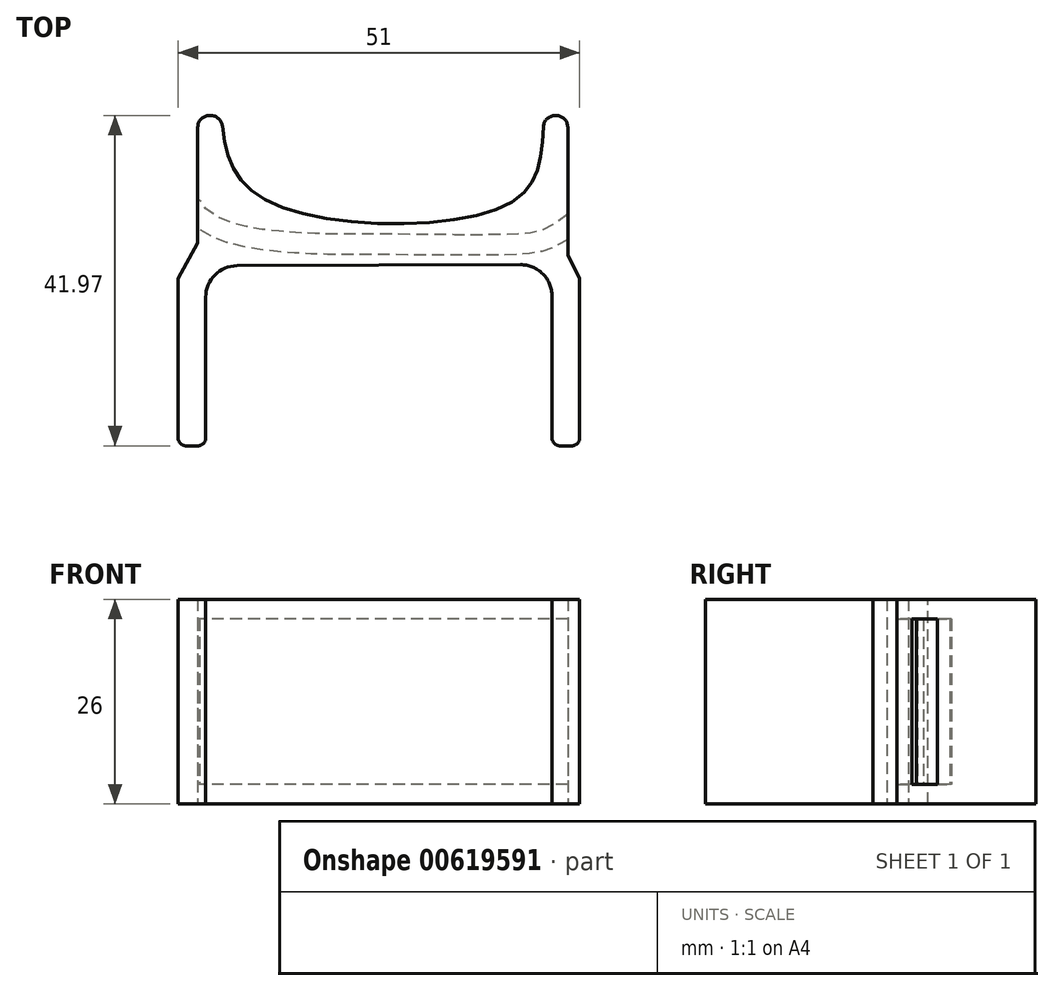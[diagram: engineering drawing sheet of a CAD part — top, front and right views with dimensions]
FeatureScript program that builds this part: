
annotation { "Feature Type Name" : "Feature", "Feature Type Description" : "" }
export const myFeature = defineFeature(function(context is Context, id is Id, definition is map)
    precondition{}
    {
        {
            var Q0;
            Q0=qCreatedBy(makeId("Top.planeOp"),FACE);
            var sketch = newSketch(context, id + "F0", { "sketchPlane" : qUnion([Q0])});
            skLineSegment(sketch, "E0.top", {"start": v(-21.5, 20.37) * mm, "end": v(19.5, 20.37) * mm});
            skPoint(sketch, "E0.middle", {"position": v(0, 0) * mm});
            skLineSegment(sketch, "E1.left", {"start": v(-15.5, 0) * mm, "end": v(-15.5, 9.44) * mm, "construction": true});
            skLineSegment(sketch, "E1.right", {"start": v(15.5, 0) * mm, "end": v(15.5, 9.44) * mm, "construction": true});
            skFitSpline(sketch, "E2", {"points": [v(19.5, 20.37) * mm, v(15.5, 9.44) * mm, v(-15.5, 9.44) * mm, v(-21.5, 20.37) * mm], "startDerivative": vector(-3.97, -51.43) * mm, "endDerivative": vector(-3.97, 51.43) * mm});
            skPoint(sketch, "E3.endSnap0", {"position": v(-22, 0) * mm});
            skLineSegment(sketch, "E4", {"start": v(-26.98, -0.36) * mm, "end": v(-26.98, -20.6) * mm});
            skLineSegment(sketch, "E5", {"start": v(-25.98, -21.6) * mm, "end": v(-24.48, -21.6) * mm});
            skLineSegment(sketch, "E6", {"start": v(24.02, -20.6) * mm, "end": v(24.02, -0.36) * mm});
            skLineSegment(sketch, "E7", {"start": v(20.52, -20.6) * mm, "end": v(20.52, -2.59) * mm});
            skLineSegment(sketch, "E8", {"start": v(16.5, 1.41) * mm, "end": v(-19.5, 1.28) * mm});
            skLineSegment(sketch, "E9", {"start": v(-23.48, -2.72) * mm, "end": v(-23.48, -20.6) * mm});
            skLineSegment(sketch, "E10.trimOffspring", {"start": v(21.52, -21.6) * mm, "end": v(23.02, -21.6) * mm});
            skPoint(sketch, "E11.visualSharp", {"position": v(-23.48, 1.26) * mm});
            skArc(sketch, "E11.filletArc", {"start": v(-19.5, 1.28) * mm, "mid": v(-22.32, 0.1) * mm, "end": v(-23.48, -2.72) * mm});
            skPoint(sketch, "E12.visualSharp", {"position": v(20.52, 1.43) * mm});
            skArc(sketch, "E12.filletArc", {"start": v(20.52, -2.59) * mm, "mid": v(19.34, 0.25) * mm, "end": v(16.5, 1.41) * mm});
            skPoint(sketch, "E13.visualSharp", {"position": v(-23.48, -21.6) * mm});
            skArc(sketch, "E13.filletArc", {"start": v(-24.48, -21.6) * mm, "mid": v(-23.78, -21.3) * mm, "end": v(-23.48, -20.6) * mm});
            skPoint(sketch, "E14.visualSharp", {"position": v(20.52, -21.6) * mm});
            skArc(sketch, "E14.filletArc", {"start": v(20.52, -20.6) * mm, "mid": v(20.8, -21.3) * mm, "end": v(21.52, -21.6) * mm});
            skPoint(sketch, "E15.visualSharp", {"position": v(-26.98, -21.6) * mm});
            skArc(sketch, "E15.filletArc", {"start": v(-26.98, -20.6) * mm, "mid": v(-26.7, -21.3) * mm, "end": v(-25.98, -21.6) * mm});
            skPoint(sketch, "E16.visualSharp", {"position": v(24.02, -21.6) * mm});
            skArc(sketch, "E16.filletArc", {"start": v(23.02, -21.6) * mm, "mid": v(23.72, -21.3) * mm, "end": v(24.02, -20.6) * mm});
            skLineSegment(sketch, "E17", {"start": v(-24.5, 4.14) * mm, "end": v(-26.98, -0.36) * mm});
            skLineSegment(sketch, "E18", {"start": v(0, 0) * mm, "end": v(0, 23.82) * mm, "construction": true});
            skLineSegment(sketch, "E19", {"start": v(22.5, 2.67) * mm, "end": v(24.02, -0.36) * mm});
            skPoint(sketch, "E20.orphan", {"position": v(-26.98, 0) * mm});
            skPoint(sketch, "E21.orphan", {"position": v(24.02, 0) * mm});
            skLineSegment(sketch, "E22", {"start": v(-21.5, 20.37) * mm, "end": v(-24.5, 20.37) * mm});
            skLineSegment(sketch, "E23", {"start": v(-24.5, 20.37) * mm, "end": v(-24.5, 4.14) * mm});
            skLineSegment(sketch, "E24", {"start": v(19.5, 20.37) * mm, "end": v(22.5, 20.37) * mm});
            skLineSegment(sketch, "E25", {"start": v(22.5, 20.37) * mm, "end": v(22.5, 2.67) * mm});
            skPoint(sketch, "E26.orphan", {"position": v(-22, 8.64) * mm});
            skPoint(sketch, "E27.orphan", {"position": v(19.53, 8.64) * mm});
            skSolve(sketch);
        }
        {
            var Q0;
            Q0=makeQuery(id+"F0.imprint","IMPRINT",FACE,{"disambiguationData":[TD([[makeQuery(id+"F0.imprint","IMPRINT",EDGE,{"derivedFrom":sQuery(id+"F0.wireOp",EDGE,"E2")}),1.0]])]});
            extrude(context, id + "F1", {"entities" : qUnion([Q0]), "endBound" : BoundingType.SYMMETRIC, "depth" : 26 * mm, "offsetDistance" : 25 * mm});
        }
        {
            var Q0;
            Q0=makeQuery(id+"F1.opExtrude","SWEPT_EDGE",EDGE,{"disambiguationData":[OSD([sQuery(id+"F0.wireOp",EDGE,"E0.top"),sQuery(id+"F0.wireOp",EDGE,"E2"),sQuery(id+"F0.wireOp",EDGE,"E22")])]});
            var Q1;
            Q1=makeQuery(id+"F1.opExtrude","SWEPT_EDGE",EDGE,{"disambiguationData":[OSD([sQuery(id+"F0.wireOp",EDGE,"E22"),sQuery(id+"F0.wireOp",EDGE,"E23")])]});
            var Q2;
            Q2=makeQuery(id+"F1.opExtrude","SWEPT_EDGE",EDGE,{"disambiguationData":[OSD([sQuery(id+"F0.wireOp",EDGE,"E24"),sQuery(id+"F0.wireOp",EDGE,"E25")])]});
            var Q3;
            Q3=makeQuery(id+"F1.opExtrude","SWEPT_EDGE",EDGE,{"disambiguationData":[OSD([sQuery(id+"F0.wireOp",EDGE,"E0.top"),sQuery(id+"F0.wireOp",EDGE,"E2"),sQuery(id+"F0.wireOp",EDGE,"E24")])]});
            fillet(context, id + "F2", {"entities" : qUnion([Q0, Q1, Q2, Q3]), "radius" : 1.5 * mm, "tangentPropagation" : true, "allowEdgeOverflow" : false});
        }
        {
            var Q0;
            Q0=qCreatedBy(makeId("Top.planeOp"),FACE);
            var sketch = newSketch(context, id + "F3", { "sketchPlane" : qUnion([Q0])});
            skFitSpline(sketch, "E28", {"points": [v(26.74, 8.34) * mm, v(15.58, 2.68) * mm, v(0, 2.68) * mm, v(-14.58, 3.1) * mm, v(-26.51, 8.34) * mm], "startDerivative": vector(-62.53, -65.11) * mm, "endDerivative": vector(-26.71, 46.77) * mm});
            skFitSpline(sketch, "E29.0", {"points": [v(24.86, 10.14) * mm, v(24.24, 9.5) * mm, v(23.1, 8.38) * mm, v(21.67, 7.18) * mm, v(20.48, 6.38) * mm, v(19.46, 5.89) * mm, v(18.53, 5.58) * mm, v(17.52, 5.4) * mm, v(16.54, 5.32) * mm, v(15.62, 5.28) * mm, v(14.63, 5.25) * mm, v(13.3, 5.22) * mm, v(11.58, 5.2) * mm, v(9.76, 5.2) * mm, v(7.25, 5.22) * mm, v(4.64, 5.24) * mm, v(2.04, 5.27) * mm, v(0.11, 5.28) * mm, v(-1.76, 5.28) * mm, v(-4.17, 5.28) * mm, v(-7.06, 5.29) * mm, v(-9.89, 5.37) * mm, v(-12.15, 5.5) * mm, v(-13.87, 5.63) * mm, v(-15.62, 5.82) * mm, v(-17.33, 6.07) * mm, v(-18.96, 6.4) * mm, v(-20.45, 6.84) * mm, v(-21.76, 7.38) * mm, v(-22.83, 8.02) * mm, v(-23.66, 8.75) * mm, v(-24.07, 9.31) * mm, v(-24.25, 9.63) * mm]});
            skLineSegment(sketch, "E30", {"start": v(-24.23, 9.6) * mm, "end": v(-26.51, 8.34) * mm});
            skLineSegment(sketch, "E31", {"start": v(24.8, 10.08) * mm, "end": v(26.74, 8.34) * mm});
            skSolve(sketch);
        }
        {
            var Q0;
            Q0 = qSketchRegion(id + "F3", true);
            extrude(context, id + "F4", {"entities" : qUnion([Q0]), "operationType" : NewBodyOperationType.REMOVE, "endBound" : BoundingType.SYMMETRIC, "depth" : 21 * mm, "offsetDistance" : 25 * mm});
        }
    });
